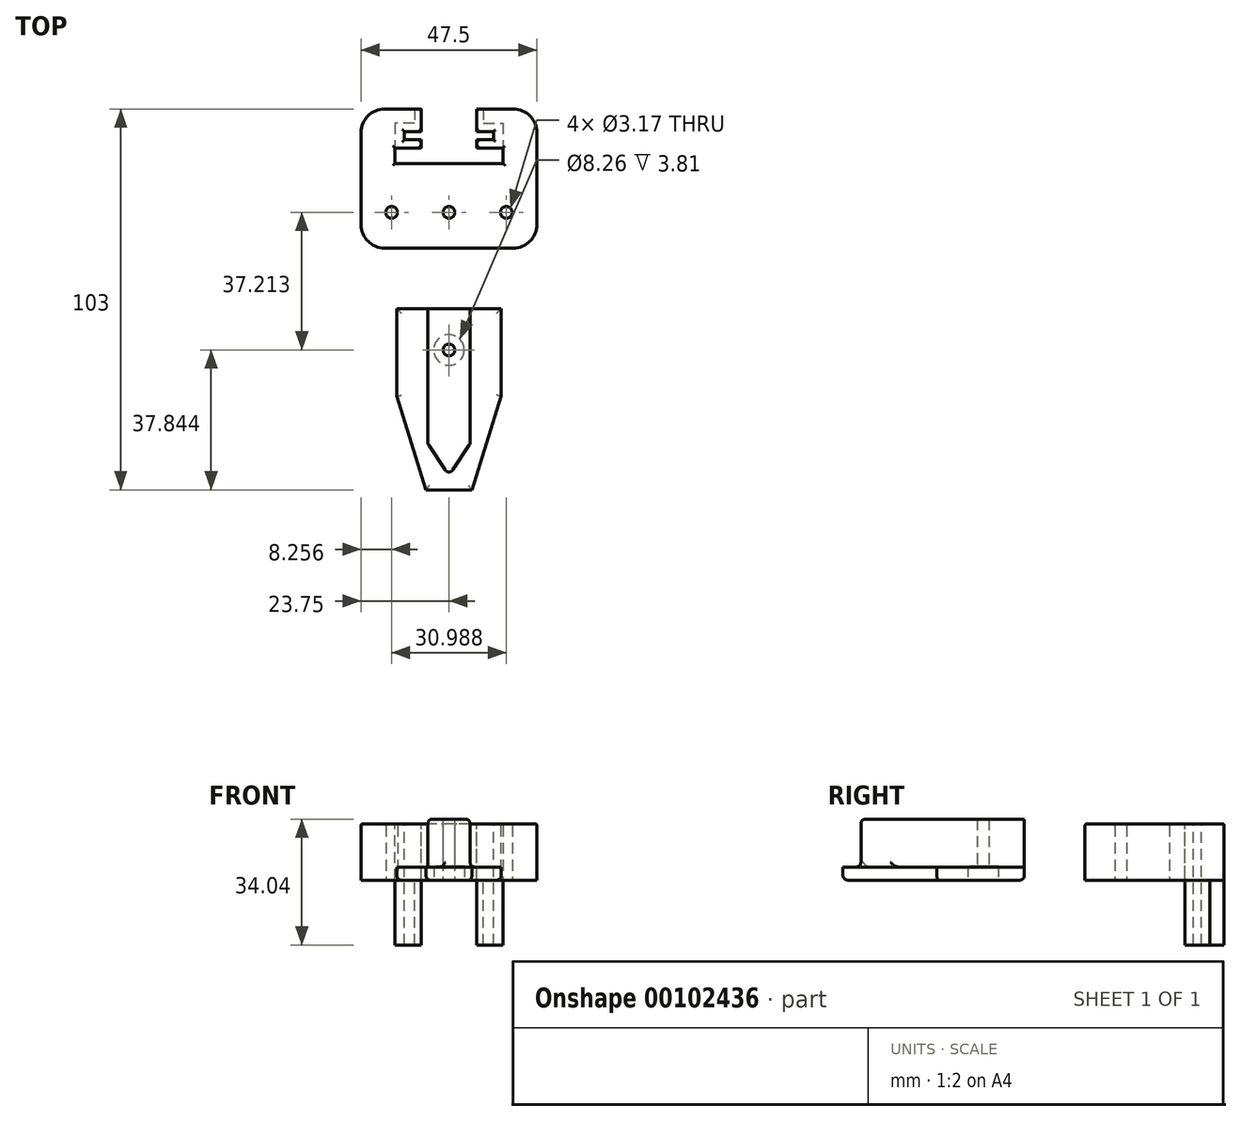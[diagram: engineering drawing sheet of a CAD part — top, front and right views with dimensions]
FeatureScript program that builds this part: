
annotation { "Feature Type Name" : "Feature", "Feature Type Description" : "" }
export const myFeature = defineFeature(function(context is Context, id is Id, definition is map)
    precondition{}
    {
        {
            var Q0;
            Q0=qCreatedBy(makeId("Top.planeOp"),FACE);
            var sketch = newSketch(context, id + "F0", { "sketchPlane" : qUnion([Q0])});
            skPoint(sketch, "E0.middle", {"position": v(0, 0) * mm});
            skLineSegment(sketch, "E1", {"start": v(-14.12, 0) * mm, "end": v(14.12, 0) * mm});
            skLineSegment(sketch, "E2", {"start": v(14.12, 0) * mm, "end": v(14.12, -23.62) * mm});
            skLineSegment(sketch, "E3", {"start": v(14.12, -23.62) * mm, "end": v(6.2, -49.02) * mm});
            skLineSegment(sketch, "E4", {"start": v(6.2, -49.02) * mm, "end": v(-6.2, -49.02) * mm});
            skLineSegment(sketch, "E5", {"start": v(-6.2, -49.02) * mm, "end": v(-14.12, -23.62) * mm});
            skLineSegment(sketch, "E6", {"start": v(-14.12, -23.62) * mm, "end": v(-14.12, 0) * mm});
            skLineSegment(sketch, "E7", {"start": v(0, 0) * mm, "end": v(0, -11.18) * mm, "construction": true});
            skCircle(sketch, "E8", {"center": v(0, -11.18) * mm, "radius": 4.13 * mm});
            skCircle(sketch, "E9", {"center": v(0, -11.18) * mm, "radius": 1.59 * mm});
            skLineSegment(sketch, "E10", {"start": v(5.71, 0) * mm, "end": v(5.71, -36.58) * mm});
            skLineSegment(sketch, "E11", {"start": v(5.72, -36.58) * mm, "end": v(0, -45.21) * mm});
            skLineSegment(sketch, "E12", {"start": v(0, -45.21) * mm, "end": v(-5.71, -36.58) * mm});
            skLineSegment(sketch, "E13", {"start": v(-5.72, -36.58) * mm, "end": v(-5.72, 0) * mm});
            skSolve(sketch);
        }
        {
            var Q0;
            {var subQ3=sQuery(id+"F0.wireOp",EDGE,"E2");Q0=makeQuery(id+"F0.imprint","IMPRINT",FACE,{"disambiguationData":[TD([[makeQuery(id+"F0.imprint","IMPRINT",EDGE,{"derivedFrom":subQ3}),-1.0]])]});}
            extrude(context, id + "F1", {"entities" : qUnion([Q0]), "depth" : 3.56 * mm});
        }
        {
            var Q0;
            Q0=makeQuery(id+"F0.imprint","IMPRINT",FACE,{"disambiguationData":[TD([[makeQuery(id+"F0.imprint","IMPRINT",EDGE,{"derivedFrom":sQuery(id+"F0.wireOp",EDGE,"E8")}),-1.0]])]});
            extrude(context, id + "F2", {"entities" : qUnion([Q0]), "operationType" : NewBodyOperationType.ADD, "depth" : 16.5 * mm});
        }
        {
            var Q0;
            Q0=makeQuery(id+"F0.imprint","IMPRINT",FACE,{"disambiguationData":[TD([[makeQuery(id+"F0.imprint","IMPRINT",EDGE,{"derivedFrom":sQuery(id+"F0.wireOp",EDGE,"E8")}),1.0]])]});
            extrude(context, id + "F3", {"entities" : qUnion([Q0]), "operationType" : NewBodyOperationType.ADD, "depth" : 16.5 * mm, "hasSecondDirection" : true, "secondDirectionOppositeDirection" : false, "secondDirectionDepth" : 3.8 * mm});
        }
        {
            var Q0;
            Q0=makeQuery(id+"F1.opExtrude","CAP_EDGE",EDGE,{"disambiguationData":[OSD([sQuery(id+"F0.wireOp",EDGE,"E4")])],"isStart":true});
            var Q1;
            Q1=makeQuery(id+"F1.opExtrude","CAP_EDGE",EDGE,{"disambiguationData":[OSD([sQuery(id+"F0.wireOp",EDGE,"E3")])],"isStart":true});
            var Q2;
            Q2=makeQuery(id+"F1.opExtrude","CAP_EDGE",EDGE,{"disambiguationData":[OSD([sQuery(id+"F0.wireOp",EDGE,"E2")])],"isStart":true});
            var Q3;
            {var subQ0=sQuery(id+"F0.wireOp",EDGE,"E1");Q3=makeQuery(id+"F2.boolean.opBoolean","MERGE",EDGE,{"derivedFrom":[makeQuery(id+"F1.opExtrude","CAP_EDGE",EDGE,{"disambiguationData":[OSD([subQ0]),TDD([makeQuery(id+"F0.imprint","IMPRINT",EDGE,{"disambiguationData":[TD([[makeQuery(id+"F0.imprint","INTERSECT",VERTEX,{"derivedFrom":[subQ0,sQuery(id+"F0.wireOp",EDGE,"E6")]}),-1.0]])],"derivedFrom":subQ0})])],"isStart":true}),makeQuery(id+"F1.opExtrude","CAP_EDGE",EDGE,{"disambiguationData":[OSD([subQ0]),TDD([makeQuery(id+"F0.imprint","IMPRINT",EDGE,{"disambiguationData":[TD([[makeQuery(id+"F0.imprint","INTERSECT",VERTEX,{"derivedFrom":[subQ0,sQuery(id+"F0.wireOp",EDGE,"E2")]}),1.0]])],"derivedFrom":subQ0})])],"isStart":true}),makeQuery(id+"F2.opExtrude","CAP_EDGE",EDGE,{"disambiguationData":[OSD([subQ0])],"isStart":true})]});}
            var Q4;
            Q4=makeQuery(id+"F1.opExtrude","CAP_EDGE",EDGE,{"disambiguationData":[OSD([sQuery(id+"F0.wireOp",EDGE,"E6")])],"isStart":true});
            var Q5;
            Q5=makeQuery(id+"F1.opExtrude","CAP_EDGE",EDGE,{"disambiguationData":[OSD([sQuery(id+"F0.wireOp",EDGE,"E5")])],"isStart":true});
            var Q6;
            Q6=makeQuery(id+"F2.opExtrude","CAP_EDGE",EDGE,{"disambiguationData":[OSD([sQuery(id+"F0.wireOp",EDGE,"E10")])],"isStart":false});
            var Q7;
            Q7=makeQuery(id+"F2.opExtrude","CAP_EDGE",EDGE,{"disambiguationData":[OSD([sQuery(id+"F0.wireOp",EDGE,"E13")])],"isStart":false});
            var Q8;
            Q8=makeQuery(id+"F2.opExtrude","SWEPT_EDGE",EDGE,{"disambiguationData":[OSD([sQuery(id+"F0.wireOp",EDGE,"E12"),sQuery(id+"F0.wireOp",EDGE,"E13")])]});
            var Q9;
            Q9=makeQuery(id+"F2.opExtrude","SWEPT_EDGE",EDGE,{"disambiguationData":[OSD([sQuery(id+"F0.wireOp",EDGE,"E10"),sQuery(id+"F0.wireOp",EDGE,"E11")])]});
            var Q10;
            Q10=makeQuery(id+"F2.opExtrude","SWEPT_FACE",FACE,{"disambiguationData":[OSD([sQuery(id+"F0.wireOp",EDGE,"E11")])]});
            var Q11;
            Q11=makeQuery(id+"F2.opExtrude","CAP_EDGE",EDGE,{"disambiguationData":[OSD([sQuery(id+"F0.wireOp",EDGE,"E12")])],"isStart":false});
            fillet(context, id + "F4", {"entities" : qUnion([Q0, Q1, Q2, Q3, Q4, Q5, Q6, Q7, Q8, Q9, Q10, Q11]), "radius" : 1.27 * mm, "tangentPropagation" : true, "allowEdgeOverflow" : false});
        }
        {
            var Q0;
            Q0=qCreatedBy(makeId("Top.planeOp"),FACE);
            var sketch = newSketch(context, id + "F5", { "sketchPlane" : qUnion([Q0])});
            skLineSegment(sketch, "E14", {"start": v(0, 16.39) * mm, "end": v(23.75, 16.39) * mm});
            skLineSegment(sketch, "E15", {"start": v(23.75, 16.39) * mm, "end": v(23.75, 53.98) * mm});
            skLineSegment(sketch, "E16", {"start": v(23.75, 53.98) * mm, "end": v(7.5, 53.98) * mm});
            skLineSegment(sketch, "E17", {"start": v(7.5, 53.98) * mm, "end": v(7.5, 47.88) * mm});
            skLineSegment(sketch, "E18", {"start": v(7.5, 47.88) * mm, "end": v(12.06, 47.88) * mm});
            skLineSegment(sketch, "E19", {"start": v(12.07, 47.88) * mm, "end": v(12.07, 45.67) * mm});
            skLineSegment(sketch, "E20", {"start": v(12.06, 45.67) * mm, "end": v(7.5, 45.67) * mm});
            skLineSegment(sketch, "E21", {"start": v(7.5, 45.67) * mm, "end": v(7.5, 43.44) * mm});
            skLineSegment(sketch, "E22", {"start": v(7.5, 43.44) * mm, "end": v(14.6, 43.44) * mm});
            skLineSegment(sketch, "E23", {"start": v(14.6, 43.44) * mm, "end": v(14.6, 39.25) * mm});
            skLineSegment(sketch, "E24", {"start": v(14.6, 39.25) * mm, "end": v(0, 39.25) * mm});
            skLineSegment(sketch, "E25", {"start": v(9.28, 53.98) * mm, "end": v(9.28, 50.17) * mm});
            skLineSegment(sketch, "E26", {"start": v(9.28, 50.17) * mm, "end": v(14.6, 50.17) * mm});
            skLineSegment(sketch, "E27", {"start": v(14.6, 50.17) * mm, "end": v(14.6, 43.44) * mm});
            skLineSegment(sketch, "E28.MirrorCS", {"start": v(23.75, 91.57) * mm, "end": v(23.75, 53.98) * mm});
            skLineSegment(sketch, "E29.MirrorCS", {"start": v(0, 91.57) * mm, "end": v(23.75, 91.57) * mm});
            skLineSegment(sketch, "E30.MirrorCS", {"start": v(0, 16.39) * mm, "end": v(-23.75, 16.39) * mm});
            skLineSegment(sketch, "E31.MirrorCS", {"start": v(-23.75, 16.39) * mm, "end": v(-23.75, 53.98) * mm});
            skLineSegment(sketch, "E32.MirrorCS", {"start": v(-23.75, 53.98) * mm, "end": v(-7.5, 53.98) * mm});
            skLineSegment(sketch, "E33.MirrorCS", {"start": v(-7.5, 53.98) * mm, "end": v(-7.5, 47.88) * mm});
            skLineSegment(sketch, "E34.MirrorCS", {"start": v(-7.5, 47.88) * mm, "end": v(-12.06, 47.88) * mm});
            skLineSegment(sketch, "E35.MirrorCS", {"start": v(-12.06, 45.67) * mm, "end": v(-7.5, 45.67) * mm});
            skLineSegment(sketch, "E36.MirrorCS", {"start": v(-7.5, 45.67) * mm, "end": v(-7.5, 43.44) * mm});
            skLineSegment(sketch, "E37.MirrorCS", {"start": v(-7.5, 43.44) * mm, "end": v(-14.6, 43.44) * mm});
            skLineSegment(sketch, "E38.MirrorCS", {"start": v(-14.6, 43.44) * mm, "end": v(-14.6, 39.25) * mm});
            skLineSegment(sketch, "E39.MirrorCS", {"start": v(-14.6, 39.25) * mm, "end": v(0, 39.25) * mm});
            skLineSegment(sketch, "E40.MirrorCS", {"start": v(-9.28, 53.98) * mm, "end": v(-9.28, 50.17) * mm});
            skLineSegment(sketch, "E41.MirrorCS", {"start": v(-9.28, 50.17) * mm, "end": v(-14.6, 50.17) * mm});
            skLineSegment(sketch, "E42.MirrorCS", {"start": v(-14.6, 50.17) * mm, "end": v(-14.6, 43.44) * mm});
            skLineSegment(sketch, "E43.MirrorCS", {"start": v(-12.07, 47.88) * mm, "end": v(-12.07, 45.67) * mm});
            skLineSegment(sketch, "E44.0", {"start": v(-17.78, 50.17) * mm, "end": v(-17.78, 43.44) * mm});
            skLineSegment(sketch, "E44.1", {"start": v(-17.78, 43.44) * mm, "end": v(-17.78, 36.07) * mm});
            skLineSegment(sketch, "E44.2", {"start": v(17.78, 50.17) * mm, "end": v(17.78, 43.44) * mm});
            skLineSegment(sketch, "E44.3", {"start": v(17.78, 43.44) * mm, "end": v(17.78, 36.07) * mm});
            skLineSegment(sketch, "E44.4", {"start": v(17.78, 36.07) * mm, "end": v(0, 36.07) * mm});
            skLineSegment(sketch, "E44.5", {"start": v(-17.78, 36.07) * mm, "end": v(0, 36.07) * mm});
            skLineSegment(sketch, "E45", {"start": v(14.6, 50.17) * mm, "end": v(17.78, 50.17) * mm});
            skLineSegment(sketch, "E46", {"start": v(-14.6, 50.17) * mm, "end": v(-17.78, 50.17) * mm});
            skLineSegment(sketch, "E47", {"start": v(0, 26.04) * mm, "end": v(15.5, 26.04) * mm, "construction": true});
            skCircle(sketch, "E48", {"center": v(0, 26.04) * mm, "radius": 1.59 * mm});
            skCircle(sketch, "E49", {"center": v(15.5, 26.04) * mm, "radius": 1.59 * mm});
            skCircle(sketch, "E50.MirrorC", {"center": v(-15.5, 26.04) * mm, "radius": 1.59 * mm});
            skSolve(sketch);
        }
        {
            var Q0;
            Q0=makeQuery(id+"F5.imprint","IMPRINT",FACE,{"disambiguationData":[TD([[makeQuery(id+"F5.imprint","IMPRINT",EDGE,{"derivedFrom":sQuery(id+"F5.wireOp",EDGE,"E14")}),1.0]])]});
            extrude(context, id + "F6", {"entities" : qUnion([Q0]), "depth" : 15.24 * mm});
        }
        {
            var Q0;
            Q0=makeQuery(id+"F5.imprint","IMPRINT",FACE,{"disambiguationData":[TD([[makeQuery(id+"F5.imprint","IMPRINT",EDGE,{"derivedFrom":sQuery(id+"F5.wireOp",EDGE,"E23")}),1.0]])]});
            extrude(context, id + "F7", {"entities" : qUnion([Q0]), "operationType" : NewBodyOperationType.ADD, "depth" : 15.24 * mm});
        }
        {
            var Q0;
            {var subQ0=sQuery(id+"F5.wireOp",EDGE,"E33.MirrorCS");Q0=makeQuery(id+"F5.imprint","IMPRINT",FACE,{"disambiguationData":[TD([[makeQuery(id+"F5.imprint","IMPRINT",EDGE,{"derivedFrom":subQ0}),-1.0]])]});}
            var Q1;
            {var subQ0=sQuery(id+"F5.wireOp",EDGE,"E17");Q1=makeQuery(id+"F5.imprint","IMPRINT",FACE,{"disambiguationData":[TD([[makeQuery(id+"F5.imprint","IMPRINT",EDGE,{"derivedFrom":subQ0}),1.0]])]});}
            extrude(context, id + "F8", {"entities" : qUnion([Q0, Q1]), "operationType" : NewBodyOperationType.ADD, "oppositeDirection" : true, "depth" : 17.53 * mm, "hasSecondDirection" : true, "secondDirectionOppositeDirection" : false, "secondDirectionDepth" : 15.24 * mm});
        }
        {
            var Q0;
            Q0=makeQuery(id+"F6.opExtrude","SWEPT_EDGE",EDGE,{"disambiguationData":[OSD([sQuery(id+"F5.wireOp",EDGE,"E15"),sQuery(id+"F5.wireOp",EDGE,"E16")])]});
            var Q1;
            Q1=makeQuery(id+"F6.opExtrude","SWEPT_EDGE",EDGE,{"disambiguationData":[OSD([sQuery(id+"F5.wireOp",EDGE,"E14"),sQuery(id+"F5.wireOp",EDGE,"E15")])]});
            var Q2;
            Q2=makeQuery(id+"F6.opExtrude","SWEPT_EDGE",EDGE,{"disambiguationData":[OSD([sQuery(id+"F5.wireOp",EDGE,"E31.MirrorCS"),sQuery(id+"F5.wireOp",EDGE,"E32.MirrorCS")])]});
            var Q3;
            Q3=makeQuery(id+"F6.opExtrude","SWEPT_EDGE",EDGE,{"disambiguationData":[OSD([sQuery(id+"F5.wireOp",EDGE,"E30.MirrorCS"),sQuery(id+"F5.wireOp",EDGE,"E31.MirrorCS")])]});
            fillet(context, id + "F9", {"entities" : qUnion([Q0, Q1, Q2, Q3]), "radius" : 6.35 * mm, "tangentPropagation" : true, "allowEdgeOverflow" : false});
        }
        {
            var Q0;
            {var subQ0=sQuery(id+"F5.wireOp",EDGE,"E16");Q0=makeQuery(id+"F8.boolean.opBoolean","MERGE",EDGE,{"derivedFrom":[makeQuery(id+"F6.opExtrude","CAP_EDGE",EDGE,{"disambiguationData":[OSD([subQ0])],"isStart":false}),makeQuery(id+"F8.opExtrude","CAP_EDGE",EDGE,{"disambiguationData":[OSD([subQ0])],"isStart":true})]});}
            var Q1;
            {var subQ0=sQuery(id+"F5.wireOp",EDGE,"E42.MirrorCS");var subQ1=sQuery(id+"F5.wireOp",EDGE,"E41.MirrorCS");var subQ2=sQuery(id+"F5.wireOp",EDGE,"E40.MirrorCS");var subQ3=sQuery(id+"F5.wireOp",EDGE,"E32.MirrorCS");var subQ4=sQuery(id+"F5.wireOp",EDGE,"E27");var subQ5=sQuery(id+"F5.wireOp",EDGE,"E26");var subQ6=sQuery(id+"F5.wireOp",EDGE,"E25");var subQ7=sQuery(id+"F5.wireOp",EDGE,"E16");var subQ8=sQuery(id+"F5.wireOp",EDGE,"E46");var subQ9=sQuery(id+"F5.wireOp",EDGE,"E45");var subQ10=sQuery(id+"F5.wireOp",EDGE,"E44.5");var subQ11=sQuery(id+"F5.wireOp",EDGE,"E44.4");var subQ12=sQuery(id+"F5.wireOp",EDGE,"E44.3");var subQ13=sQuery(id+"F5.wireOp",EDGE,"E44.2");var subQ14=sQuery(id+"F5.wireOp",EDGE,"E44.1");var subQ15=sQuery(id+"F5.wireOp",EDGE,"E44.0");var subQ16=sQuery(id+"F5.wireOp",EDGE,"E15");Q1=makeQuery(id+"F9.opFillet","BLEND_EDGE",EDGE,{"blendedFrom":[makeQuery(id+"F6.opExtrude","SWEPT_EDGE",EDGE,{"disambiguationData":[OSD([subQ16,subQ7])]}),makeQuery(id+"F8.boolean.opBoolean","MERGE",FACE,{"derivedFrom":[makeQuery(id+"F7.boolean.opBoolean","MERGE",FACE,{"derivedFrom":[makeQuery(id+"F6.opExtrude","CAP_FACE",FACE,{"disambiguationData":[OSD([sQuery(id+"F5.wireOp",EDGE,"E14"),subQ16,subQ7,subQ6,subQ5,sQuery(id+"F5.wireOp",EDGE,"E30.MirrorCS"),sQuery(id+"F5.wireOp",EDGE,"E31.MirrorCS"),subQ3,subQ2,subQ1,subQ15,subQ14,subQ13,subQ12,subQ11,subQ10,subQ9,subQ8,sQuery(id+"F5.wireOp",EDGE,"E48"),sQuery(id+"F5.wireOp",EDGE,"E49"),sQuery(id+"F5.wireOp",EDGE,"E50.MirrorC")])],"isStart":false}),makeQuery(id+"F7.opExtrude","CAP_FACE",FACE,{"disambiguationData":[OSD([sQuery(id+"F5.wireOp",EDGE,"E23"),sQuery(id+"F5.wireOp",EDGE,"E24"),subQ4,sQuery(id+"F5.wireOp",EDGE,"E38.MirrorCS"),sQuery(id+"F5.wireOp",EDGE,"E39.MirrorCS"),subQ0,subQ15,subQ14,subQ13,subQ12,subQ11,subQ10,subQ9,subQ8])],"isStart":false})]}),makeQuery(id+"F8.opExtrude","CAP_FACE",FACE,{"disambiguationData":[OSD([subQ7,sQuery(id+"F5.wireOp",EDGE,"E17"),sQuery(id+"F5.wireOp",EDGE,"E18"),sQuery(id+"F5.wireOp",EDGE,"E19"),sQuery(id+"F5.wireOp",EDGE,"E20"),sQuery(id+"F5.wireOp",EDGE,"E21"),sQuery(id+"F5.wireOp",EDGE,"E22"),subQ6,subQ5,subQ4])],"isStart":true}),makeQuery(id+"F8.opExtrude","CAP_FACE",FACE,{"disambiguationData":[OSD([subQ3,sQuery(id+"F5.wireOp",EDGE,"E33.MirrorCS"),sQuery(id+"F5.wireOp",EDGE,"E34.MirrorCS"),sQuery(id+"F5.wireOp",EDGE,"E35.MirrorCS"),sQuery(id+"F5.wireOp",EDGE,"E36.MirrorCS"),sQuery(id+"F5.wireOp",EDGE,"E37.MirrorCS"),subQ2,subQ1,subQ0,sQuery(id+"F5.wireOp",EDGE,"E43.MirrorCS")])],"isStart":true})]})],"blendedInto":[makeQuery(id+"F8.boolean.opBoolean","MERGE",FACE,{"derivedFrom":[makeQuery(id+"F7.boolean.opBoolean","MERGE",FACE,{"derivedFrom":[makeQuery(id+"F6.opExtrude","CAP_FACE",FACE,{"disambiguationData":[OSD([sQuery(id+"F5.wireOp",EDGE,"E14"),subQ16,subQ7,subQ6,subQ5,sQuery(id+"F5.wireOp",EDGE,"E30.MirrorCS"),sQuery(id+"F5.wireOp",EDGE,"E31.MirrorCS"),subQ3,subQ2,subQ1,subQ15,subQ14,subQ13,subQ12,subQ11,subQ10,subQ9,subQ8,sQuery(id+"F5.wireOp",EDGE,"E48"),sQuery(id+"F5.wireOp",EDGE,"E49"),sQuery(id+"F5.wireOp",EDGE,"E50.MirrorC")])],"isStart":false}),makeQuery(id+"F7.opExtrude","CAP_FACE",FACE,{"disambiguationData":[OSD([sQuery(id+"F5.wireOp",EDGE,"E23"),sQuery(id+"F5.wireOp",EDGE,"E24"),subQ4,sQuery(id+"F5.wireOp",EDGE,"E38.MirrorCS"),sQuery(id+"F5.wireOp",EDGE,"E39.MirrorCS"),subQ0,subQ15,subQ14,subQ13,subQ12,subQ11,subQ10,subQ9,subQ8])],"isStart":false})]}),makeQuery(id+"F8.opExtrude","CAP_FACE",FACE,{"disambiguationData":[OSD([subQ7,sQuery(id+"F5.wireOp",EDGE,"E17"),sQuery(id+"F5.wireOp",EDGE,"E18"),sQuery(id+"F5.wireOp",EDGE,"E19"),sQuery(id+"F5.wireOp",EDGE,"E20"),sQuery(id+"F5.wireOp",EDGE,"E21"),sQuery(id+"F5.wireOp",EDGE,"E22"),subQ6,subQ5,subQ4])],"isStart":true}),makeQuery(id+"F8.opExtrude","CAP_FACE",FACE,{"disambiguationData":[OSD([subQ3,sQuery(id+"F5.wireOp",EDGE,"E33.MirrorCS"),sQuery(id+"F5.wireOp",EDGE,"E34.MirrorCS"),sQuery(id+"F5.wireOp",EDGE,"E35.MirrorCS"),sQuery(id+"F5.wireOp",EDGE,"E36.MirrorCS"),sQuery(id+"F5.wireOp",EDGE,"E37.MirrorCS"),subQ2,subQ1,subQ0,sQuery(id+"F5.wireOp",EDGE,"E43.MirrorCS")])],"isStart":true})]})]});}
            var Q2;
            Q2=makeQuery(id+"F6.opExtrude","CAP_EDGE",EDGE,{"disambiguationData":[OSD([sQuery(id+"F5.wireOp",EDGE,"E15")])],"isStart":false});
            var Q3;
            {var subQ0=sQuery(id+"F5.wireOp",EDGE,"E42.MirrorCS");var subQ1=sQuery(id+"F5.wireOp",EDGE,"E41.MirrorCS");var subQ2=sQuery(id+"F5.wireOp",EDGE,"E40.MirrorCS");var subQ3=sQuery(id+"F5.wireOp",EDGE,"E32.MirrorCS");var subQ4=sQuery(id+"F5.wireOp",EDGE,"E27");var subQ5=sQuery(id+"F5.wireOp",EDGE,"E26");var subQ6=sQuery(id+"F5.wireOp",EDGE,"E25");var subQ7=sQuery(id+"F5.wireOp",EDGE,"E16");var subQ8=sQuery(id+"F5.wireOp",EDGE,"E46");var subQ9=sQuery(id+"F5.wireOp",EDGE,"E45");var subQ10=sQuery(id+"F5.wireOp",EDGE,"E44.5");var subQ11=sQuery(id+"F5.wireOp",EDGE,"E44.4");var subQ12=sQuery(id+"F5.wireOp",EDGE,"E44.3");var subQ13=sQuery(id+"F5.wireOp",EDGE,"E44.2");var subQ14=sQuery(id+"F5.wireOp",EDGE,"E44.1");var subQ15=sQuery(id+"F5.wireOp",EDGE,"E44.0");var subQ16=sQuery(id+"F5.wireOp",EDGE,"E15");var subQ17=sQuery(id+"F5.wireOp",EDGE,"E14");Q3=makeQuery(id+"F9.opFillet","BLEND_EDGE",EDGE,{"blendedFrom":[makeQuery(id+"F6.opExtrude","SWEPT_EDGE",EDGE,{"disambiguationData":[OSD([subQ17,subQ16])]}),makeQuery(id+"F8.boolean.opBoolean","MERGE",FACE,{"derivedFrom":[makeQuery(id+"F7.boolean.opBoolean","MERGE",FACE,{"derivedFrom":[makeQuery(id+"F6.opExtrude","CAP_FACE",FACE,{"disambiguationData":[OSD([subQ17,subQ16,subQ7,subQ6,subQ5,sQuery(id+"F5.wireOp",EDGE,"E30.MirrorCS"),sQuery(id+"F5.wireOp",EDGE,"E31.MirrorCS"),subQ3,subQ2,subQ1,subQ15,subQ14,subQ13,subQ12,subQ11,subQ10,subQ9,subQ8,sQuery(id+"F5.wireOp",EDGE,"E48"),sQuery(id+"F5.wireOp",EDGE,"E49"),sQuery(id+"F5.wireOp",EDGE,"E50.MirrorC")])],"isStart":false}),makeQuery(id+"F7.opExtrude","CAP_FACE",FACE,{"disambiguationData":[OSD([sQuery(id+"F5.wireOp",EDGE,"E23"),sQuery(id+"F5.wireOp",EDGE,"E24"),subQ4,sQuery(id+"F5.wireOp",EDGE,"E38.MirrorCS"),sQuery(id+"F5.wireOp",EDGE,"E39.MirrorCS"),subQ0,subQ15,subQ14,subQ13,subQ12,subQ11,subQ10,subQ9,subQ8])],"isStart":false})]}),makeQuery(id+"F8.opExtrude","CAP_FACE",FACE,{"disambiguationData":[OSD([subQ7,sQuery(id+"F5.wireOp",EDGE,"E17"),sQuery(id+"F5.wireOp",EDGE,"E18"),sQuery(id+"F5.wireOp",EDGE,"E19"),sQuery(id+"F5.wireOp",EDGE,"E20"),sQuery(id+"F5.wireOp",EDGE,"E21"),sQuery(id+"F5.wireOp",EDGE,"E22"),subQ6,subQ5,subQ4])],"isStart":true}),makeQuery(id+"F8.opExtrude","CAP_FACE",FACE,{"disambiguationData":[OSD([subQ3,sQuery(id+"F5.wireOp",EDGE,"E33.MirrorCS"),sQuery(id+"F5.wireOp",EDGE,"E34.MirrorCS"),sQuery(id+"F5.wireOp",EDGE,"E35.MirrorCS"),sQuery(id+"F5.wireOp",EDGE,"E36.MirrorCS"),sQuery(id+"F5.wireOp",EDGE,"E37.MirrorCS"),subQ2,subQ1,subQ0,sQuery(id+"F5.wireOp",EDGE,"E43.MirrorCS")])],"isStart":true})]})],"blendedInto":[makeQuery(id+"F8.boolean.opBoolean","MERGE",FACE,{"derivedFrom":[makeQuery(id+"F7.boolean.opBoolean","MERGE",FACE,{"derivedFrom":[makeQuery(id+"F6.opExtrude","CAP_FACE",FACE,{"disambiguationData":[OSD([subQ17,subQ16,subQ7,subQ6,subQ5,sQuery(id+"F5.wireOp",EDGE,"E30.MirrorCS"),sQuery(id+"F5.wireOp",EDGE,"E31.MirrorCS"),subQ3,subQ2,subQ1,subQ15,subQ14,subQ13,subQ12,subQ11,subQ10,subQ9,subQ8,sQuery(id+"F5.wireOp",EDGE,"E48"),sQuery(id+"F5.wireOp",EDGE,"E49"),sQuery(id+"F5.wireOp",EDGE,"E50.MirrorC")])],"isStart":false}),makeQuery(id+"F7.opExtrude","CAP_FACE",FACE,{"disambiguationData":[OSD([sQuery(id+"F5.wireOp",EDGE,"E23"),sQuery(id+"F5.wireOp",EDGE,"E24"),subQ4,sQuery(id+"F5.wireOp",EDGE,"E38.MirrorCS"),sQuery(id+"F5.wireOp",EDGE,"E39.MirrorCS"),subQ0,subQ15,subQ14,subQ13,subQ12,subQ11,subQ10,subQ9,subQ8])],"isStart":false})]}),makeQuery(id+"F8.opExtrude","CAP_FACE",FACE,{"disambiguationData":[OSD([subQ7,sQuery(id+"F5.wireOp",EDGE,"E17"),sQuery(id+"F5.wireOp",EDGE,"E18"),sQuery(id+"F5.wireOp",EDGE,"E19"),sQuery(id+"F5.wireOp",EDGE,"E20"),sQuery(id+"F5.wireOp",EDGE,"E21"),sQuery(id+"F5.wireOp",EDGE,"E22"),subQ6,subQ5,subQ4])],"isStart":true}),makeQuery(id+"F8.opExtrude","CAP_FACE",FACE,{"disambiguationData":[OSD([subQ3,sQuery(id+"F5.wireOp",EDGE,"E33.MirrorCS"),sQuery(id+"F5.wireOp",EDGE,"E34.MirrorCS"),sQuery(id+"F5.wireOp",EDGE,"E35.MirrorCS"),sQuery(id+"F5.wireOp",EDGE,"E36.MirrorCS"),sQuery(id+"F5.wireOp",EDGE,"E37.MirrorCS"),subQ2,subQ1,subQ0,sQuery(id+"F5.wireOp",EDGE,"E43.MirrorCS")])],"isStart":true})]})]});}
            var Q4;
            Q4=makeQuery(id+"F6.opExtrude","CAP_EDGE",EDGE,{"disambiguationData":[OSD([sQuery(id+"F5.wireOp",EDGE,"E14"),sQuery(id+"F5.wireOp",EDGE,"E30.MirrorCS")])],"isStart":false});
            var Q5;
            {var subQ0=sQuery(id+"F5.wireOp",EDGE,"E42.MirrorCS");var subQ1=sQuery(id+"F5.wireOp",EDGE,"E41.MirrorCS");var subQ2=sQuery(id+"F5.wireOp",EDGE,"E40.MirrorCS");var subQ3=sQuery(id+"F5.wireOp",EDGE,"E32.MirrorCS");var subQ4=sQuery(id+"F5.wireOp",EDGE,"E27");var subQ5=sQuery(id+"F5.wireOp",EDGE,"E26");var subQ6=sQuery(id+"F5.wireOp",EDGE,"E25");var subQ7=sQuery(id+"F5.wireOp",EDGE,"E16");var subQ8=sQuery(id+"F5.wireOp",EDGE,"E46");var subQ9=sQuery(id+"F5.wireOp",EDGE,"E45");var subQ10=sQuery(id+"F5.wireOp",EDGE,"E44.5");var subQ11=sQuery(id+"F5.wireOp",EDGE,"E44.4");var subQ12=sQuery(id+"F5.wireOp",EDGE,"E44.3");var subQ13=sQuery(id+"F5.wireOp",EDGE,"E44.2");var subQ14=sQuery(id+"F5.wireOp",EDGE,"E44.1");var subQ15=sQuery(id+"F5.wireOp",EDGE,"E44.0");var subQ16=sQuery(id+"F5.wireOp",EDGE,"E31.MirrorCS");var subQ17=sQuery(id+"F5.wireOp",EDGE,"E30.MirrorCS");Q5=makeQuery(id+"F9.opFillet","BLEND_EDGE",EDGE,{"blendedFrom":[makeQuery(id+"F6.opExtrude","SWEPT_EDGE",EDGE,{"disambiguationData":[OSD([subQ17,subQ16])]}),makeQuery(id+"F8.boolean.opBoolean","MERGE",FACE,{"derivedFrom":[makeQuery(id+"F7.boolean.opBoolean","MERGE",FACE,{"derivedFrom":[makeQuery(id+"F6.opExtrude","CAP_FACE",FACE,{"disambiguationData":[OSD([sQuery(id+"F5.wireOp",EDGE,"E14"),sQuery(id+"F5.wireOp",EDGE,"E15"),subQ7,subQ6,subQ5,subQ17,subQ16,subQ3,subQ2,subQ1,subQ15,subQ14,subQ13,subQ12,subQ11,subQ10,subQ9,subQ8,sQuery(id+"F5.wireOp",EDGE,"E48"),sQuery(id+"F5.wireOp",EDGE,"E49"),sQuery(id+"F5.wireOp",EDGE,"E50.MirrorC")])],"isStart":false}),makeQuery(id+"F7.opExtrude","CAP_FACE",FACE,{"disambiguationData":[OSD([sQuery(id+"F5.wireOp",EDGE,"E23"),sQuery(id+"F5.wireOp",EDGE,"E24"),subQ4,sQuery(id+"F5.wireOp",EDGE,"E38.MirrorCS"),sQuery(id+"F5.wireOp",EDGE,"E39.MirrorCS"),subQ0,subQ15,subQ14,subQ13,subQ12,subQ11,subQ10,subQ9,subQ8])],"isStart":false})]}),makeQuery(id+"F8.opExtrude","CAP_FACE",FACE,{"disambiguationData":[OSD([subQ7,sQuery(id+"F5.wireOp",EDGE,"E17"),sQuery(id+"F5.wireOp",EDGE,"E18"),sQuery(id+"F5.wireOp",EDGE,"E19"),sQuery(id+"F5.wireOp",EDGE,"E20"),sQuery(id+"F5.wireOp",EDGE,"E21"),sQuery(id+"F5.wireOp",EDGE,"E22"),subQ6,subQ5,subQ4])],"isStart":true}),makeQuery(id+"F8.opExtrude","CAP_FACE",FACE,{"disambiguationData":[OSD([subQ3,sQuery(id+"F5.wireOp",EDGE,"E33.MirrorCS"),sQuery(id+"F5.wireOp",EDGE,"E34.MirrorCS"),sQuery(id+"F5.wireOp",EDGE,"E35.MirrorCS"),sQuery(id+"F5.wireOp",EDGE,"E36.MirrorCS"),sQuery(id+"F5.wireOp",EDGE,"E37.MirrorCS"),subQ2,subQ1,subQ0,sQuery(id+"F5.wireOp",EDGE,"E43.MirrorCS")])],"isStart":true})]})],"blendedInto":[makeQuery(id+"F8.boolean.opBoolean","MERGE",FACE,{"derivedFrom":[makeQuery(id+"F7.boolean.opBoolean","MERGE",FACE,{"derivedFrom":[makeQuery(id+"F6.opExtrude","CAP_FACE",FACE,{"disambiguationData":[OSD([sQuery(id+"F5.wireOp",EDGE,"E14"),sQuery(id+"F5.wireOp",EDGE,"E15"),subQ7,subQ6,subQ5,subQ17,subQ16,subQ3,subQ2,subQ1,subQ15,subQ14,subQ13,subQ12,subQ11,subQ10,subQ9,subQ8,sQuery(id+"F5.wireOp",EDGE,"E48"),sQuery(id+"F5.wireOp",EDGE,"E49"),sQuery(id+"F5.wireOp",EDGE,"E50.MirrorC")])],"isStart":false}),makeQuery(id+"F7.opExtrude","CAP_FACE",FACE,{"disambiguationData":[OSD([sQuery(id+"F5.wireOp",EDGE,"E23"),sQuery(id+"F5.wireOp",EDGE,"E24"),subQ4,sQuery(id+"F5.wireOp",EDGE,"E38.MirrorCS"),sQuery(id+"F5.wireOp",EDGE,"E39.MirrorCS"),subQ0,subQ15,subQ14,subQ13,subQ12,subQ11,subQ10,subQ9,subQ8])],"isStart":false})]}),makeQuery(id+"F8.opExtrude","CAP_FACE",FACE,{"disambiguationData":[OSD([subQ7,sQuery(id+"F5.wireOp",EDGE,"E17"),sQuery(id+"F5.wireOp",EDGE,"E18"),sQuery(id+"F5.wireOp",EDGE,"E19"),sQuery(id+"F5.wireOp",EDGE,"E20"),sQuery(id+"F5.wireOp",EDGE,"E21"),sQuery(id+"F5.wireOp",EDGE,"E22"),subQ6,subQ5,subQ4])],"isStart":true}),makeQuery(id+"F8.opExtrude","CAP_FACE",FACE,{"disambiguationData":[OSD([subQ3,sQuery(id+"F5.wireOp",EDGE,"E33.MirrorCS"),sQuery(id+"F5.wireOp",EDGE,"E34.MirrorCS"),sQuery(id+"F5.wireOp",EDGE,"E35.MirrorCS"),sQuery(id+"F5.wireOp",EDGE,"E36.MirrorCS"),sQuery(id+"F5.wireOp",EDGE,"E37.MirrorCS"),subQ2,subQ1,subQ0,sQuery(id+"F5.wireOp",EDGE,"E43.MirrorCS")])],"isStart":true})]})]});}
            var Q6;
            Q6=makeQuery(id+"F6.opExtrude","CAP_EDGE",EDGE,{"disambiguationData":[OSD([sQuery(id+"F5.wireOp",EDGE,"E31.MirrorCS")])],"isStart":false});
            var Q7;
            {var subQ0=sQuery(id+"F5.wireOp",EDGE,"E42.MirrorCS");var subQ1=sQuery(id+"F5.wireOp",EDGE,"E41.MirrorCS");var subQ2=sQuery(id+"F5.wireOp",EDGE,"E40.MirrorCS");var subQ3=sQuery(id+"F5.wireOp",EDGE,"E32.MirrorCS");var subQ4=sQuery(id+"F5.wireOp",EDGE,"E27");var subQ5=sQuery(id+"F5.wireOp",EDGE,"E26");var subQ6=sQuery(id+"F5.wireOp",EDGE,"E25");var subQ7=sQuery(id+"F5.wireOp",EDGE,"E16");var subQ8=sQuery(id+"F5.wireOp",EDGE,"E46");var subQ9=sQuery(id+"F5.wireOp",EDGE,"E45");var subQ10=sQuery(id+"F5.wireOp",EDGE,"E44.5");var subQ11=sQuery(id+"F5.wireOp",EDGE,"E44.4");var subQ12=sQuery(id+"F5.wireOp",EDGE,"E44.3");var subQ13=sQuery(id+"F5.wireOp",EDGE,"E44.2");var subQ14=sQuery(id+"F5.wireOp",EDGE,"E44.1");var subQ15=sQuery(id+"F5.wireOp",EDGE,"E44.0");var subQ16=sQuery(id+"F5.wireOp",EDGE,"E31.MirrorCS");Q7=makeQuery(id+"F9.opFillet","BLEND_EDGE",EDGE,{"blendedFrom":[makeQuery(id+"F6.opExtrude","SWEPT_EDGE",EDGE,{"disambiguationData":[OSD([subQ16,subQ3])]}),makeQuery(id+"F8.boolean.opBoolean","MERGE",FACE,{"derivedFrom":[makeQuery(id+"F7.boolean.opBoolean","MERGE",FACE,{"derivedFrom":[makeQuery(id+"F6.opExtrude","CAP_FACE",FACE,{"disambiguationData":[OSD([sQuery(id+"F5.wireOp",EDGE,"E14"),sQuery(id+"F5.wireOp",EDGE,"E15"),subQ7,subQ6,subQ5,sQuery(id+"F5.wireOp",EDGE,"E30.MirrorCS"),subQ16,subQ3,subQ2,subQ1,subQ15,subQ14,subQ13,subQ12,subQ11,subQ10,subQ9,subQ8,sQuery(id+"F5.wireOp",EDGE,"E48"),sQuery(id+"F5.wireOp",EDGE,"E49"),sQuery(id+"F5.wireOp",EDGE,"E50.MirrorC")])],"isStart":false}),makeQuery(id+"F7.opExtrude","CAP_FACE",FACE,{"disambiguationData":[OSD([sQuery(id+"F5.wireOp",EDGE,"E23"),sQuery(id+"F5.wireOp",EDGE,"E24"),subQ4,sQuery(id+"F5.wireOp",EDGE,"E38.MirrorCS"),sQuery(id+"F5.wireOp",EDGE,"E39.MirrorCS"),subQ0,subQ15,subQ14,subQ13,subQ12,subQ11,subQ10,subQ9,subQ8])],"isStart":false})]}),makeQuery(id+"F8.opExtrude","CAP_FACE",FACE,{"disambiguationData":[OSD([subQ7,sQuery(id+"F5.wireOp",EDGE,"E17"),sQuery(id+"F5.wireOp",EDGE,"E18"),sQuery(id+"F5.wireOp",EDGE,"E19"),sQuery(id+"F5.wireOp",EDGE,"E20"),sQuery(id+"F5.wireOp",EDGE,"E21"),sQuery(id+"F5.wireOp",EDGE,"E22"),subQ6,subQ5,subQ4])],"isStart":true}),makeQuery(id+"F8.opExtrude","CAP_FACE",FACE,{"disambiguationData":[OSD([subQ3,sQuery(id+"F5.wireOp",EDGE,"E33.MirrorCS"),sQuery(id+"F5.wireOp",EDGE,"E34.MirrorCS"),sQuery(id+"F5.wireOp",EDGE,"E35.MirrorCS"),sQuery(id+"F5.wireOp",EDGE,"E36.MirrorCS"),sQuery(id+"F5.wireOp",EDGE,"E37.MirrorCS"),subQ2,subQ1,subQ0,sQuery(id+"F5.wireOp",EDGE,"E43.MirrorCS")])],"isStart":true})]})],"blendedInto":[makeQuery(id+"F8.boolean.opBoolean","MERGE",FACE,{"derivedFrom":[makeQuery(id+"F7.boolean.opBoolean","MERGE",FACE,{"derivedFrom":[makeQuery(id+"F6.opExtrude","CAP_FACE",FACE,{"disambiguationData":[OSD([sQuery(id+"F5.wireOp",EDGE,"E14"),sQuery(id+"F5.wireOp",EDGE,"E15"),subQ7,subQ6,subQ5,sQuery(id+"F5.wireOp",EDGE,"E30.MirrorCS"),subQ16,subQ3,subQ2,subQ1,subQ15,subQ14,subQ13,subQ12,subQ11,subQ10,subQ9,subQ8,sQuery(id+"F5.wireOp",EDGE,"E48"),sQuery(id+"F5.wireOp",EDGE,"E49"),sQuery(id+"F5.wireOp",EDGE,"E50.MirrorC")])],"isStart":false}),makeQuery(id+"F7.opExtrude","CAP_FACE",FACE,{"disambiguationData":[OSD([sQuery(id+"F5.wireOp",EDGE,"E23"),sQuery(id+"F5.wireOp",EDGE,"E24"),subQ4,sQuery(id+"F5.wireOp",EDGE,"E38.MirrorCS"),sQuery(id+"F5.wireOp",EDGE,"E39.MirrorCS"),subQ0,subQ15,subQ14,subQ13,subQ12,subQ11,subQ10,subQ9,subQ8])],"isStart":false})]}),makeQuery(id+"F8.opExtrude","CAP_FACE",FACE,{"disambiguationData":[OSD([subQ7,sQuery(id+"F5.wireOp",EDGE,"E17"),sQuery(id+"F5.wireOp",EDGE,"E18"),sQuery(id+"F5.wireOp",EDGE,"E19"),sQuery(id+"F5.wireOp",EDGE,"E20"),sQuery(id+"F5.wireOp",EDGE,"E21"),sQuery(id+"F5.wireOp",EDGE,"E22"),subQ6,subQ5,subQ4])],"isStart":true}),makeQuery(id+"F8.opExtrude","CAP_FACE",FACE,{"disambiguationData":[OSD([subQ3,sQuery(id+"F5.wireOp",EDGE,"E33.MirrorCS"),sQuery(id+"F5.wireOp",EDGE,"E34.MirrorCS"),sQuery(id+"F5.wireOp",EDGE,"E35.MirrorCS"),sQuery(id+"F5.wireOp",EDGE,"E36.MirrorCS"),sQuery(id+"F5.wireOp",EDGE,"E37.MirrorCS"),subQ2,subQ1,subQ0,sQuery(id+"F5.wireOp",EDGE,"E43.MirrorCS")])],"isStart":true})]})]});}
            var Q8;
            Q8=makeQuery(id+"F7.opExtrude","CAP_EDGE",EDGE,{"disambiguationData":[OSD([sQuery(id+"F5.wireOp",EDGE,"E38.MirrorCS"),sQuery(id+"F5.wireOp",EDGE,"E42.MirrorCS")])],"isStart":false});
            var Q9;
            Q9=makeQuery(id+"F7.opExtrude","CAP_EDGE",EDGE,{"disambiguationData":[OSD([sQuery(id+"F5.wireOp",EDGE,"E24"),sQuery(id+"F5.wireOp",EDGE,"E39.MirrorCS")])],"isStart":false});
            var Q10;
            Q10=makeQuery(id+"F7.opExtrude","CAP_EDGE",EDGE,{"disambiguationData":[OSD([sQuery(id+"F5.wireOp",EDGE,"E23"),sQuery(id+"F5.wireOp",EDGE,"E27")])],"isStart":false});
            var Q11;
            Q11=makeQuery(id+"F8.opExtrude","CAP_EDGE",EDGE,{"disambiguationData":[OSD([sQuery(id+"F5.wireOp",EDGE,"E22")])],"isStart":true});
            var Q12;
            Q12=makeQuery(id+"F8.opExtrude","CAP_EDGE",EDGE,{"disambiguationData":[OSD([sQuery(id+"F5.wireOp",EDGE,"E37.MirrorCS")])],"isStart":true});
            var Q13;
            Q13=makeQuery(id+"F8.opExtrude","CAP_EDGE",EDGE,{"disambiguationData":[OSD([sQuery(id+"F5.wireOp",EDGE,"E36.MirrorCS")])],"isStart":true});
            var Q14;
            {var subQ0=sQuery(id+"F5.wireOp",EDGE,"E42.MirrorCS");var subQ1=sQuery(id+"F5.wireOp",EDGE,"E41.MirrorCS");var subQ2=sQuery(id+"F5.wireOp",EDGE,"E40.MirrorCS");var subQ3=sQuery(id+"F5.wireOp",EDGE,"E32.MirrorCS");var subQ4=sQuery(id+"F5.wireOp",EDGE,"E27");var subQ5=sQuery(id+"F5.wireOp",EDGE,"E26");var subQ6=sQuery(id+"F5.wireOp",EDGE,"E25");var subQ7=sQuery(id+"F5.wireOp",EDGE,"E16");var subQ8=sQuery(id+"F5.wireOp",EDGE,"E46");var subQ9=sQuery(id+"F5.wireOp",EDGE,"E45");var subQ10=sQuery(id+"F5.wireOp",EDGE,"E44.5");var subQ11=sQuery(id+"F5.wireOp",EDGE,"E44.4");var subQ12=sQuery(id+"F5.wireOp",EDGE,"E44.3");var subQ13=sQuery(id+"F5.wireOp",EDGE,"E44.2");var subQ14=sQuery(id+"F5.wireOp",EDGE,"E44.1");var subQ15=sQuery(id+"F5.wireOp",EDGE,"E44.0");Q14=makeQuery(id+"F8.boolean.opBoolean","MERGE",FACE,{"derivedFrom":[makeQuery(id+"F7.boolean.opBoolean","MERGE",FACE,{"derivedFrom":[makeQuery(id+"F6.opExtrude","CAP_FACE",FACE,{"disambiguationData":[OSD([sQuery(id+"F5.wireOp",EDGE,"E14"),sQuery(id+"F5.wireOp",EDGE,"E15"),subQ7,subQ6,subQ5,sQuery(id+"F5.wireOp",EDGE,"E30.MirrorCS"),sQuery(id+"F5.wireOp",EDGE,"E31.MirrorCS"),subQ3,subQ2,subQ1,subQ15,subQ14,subQ13,subQ12,subQ11,subQ10,subQ9,subQ8,sQuery(id+"F5.wireOp",EDGE,"E48"),sQuery(id+"F5.wireOp",EDGE,"E49"),sQuery(id+"F5.wireOp",EDGE,"E50.MirrorC")])],"isStart":false}),makeQuery(id+"F7.opExtrude","CAP_FACE",FACE,{"disambiguationData":[OSD([sQuery(id+"F5.wireOp",EDGE,"E23"),sQuery(id+"F5.wireOp",EDGE,"E24"),subQ4,sQuery(id+"F5.wireOp",EDGE,"E38.MirrorCS"),sQuery(id+"F5.wireOp",EDGE,"E39.MirrorCS"),subQ0,subQ15,subQ14,subQ13,subQ12,subQ11,subQ10,subQ9,subQ8])],"isStart":false})]}),makeQuery(id+"F8.opExtrude","CAP_FACE",FACE,{"disambiguationData":[OSD([subQ7,sQuery(id+"F5.wireOp",EDGE,"E17"),sQuery(id+"F5.wireOp",EDGE,"E18"),sQuery(id+"F5.wireOp",EDGE,"E19"),sQuery(id+"F5.wireOp",EDGE,"E20"),sQuery(id+"F5.wireOp",EDGE,"E21"),sQuery(id+"F5.wireOp",EDGE,"E22"),subQ6,subQ5,subQ4])],"isStart":true}),makeQuery(id+"F8.opExtrude","CAP_FACE",FACE,{"disambiguationData":[OSD([subQ3,sQuery(id+"F5.wireOp",EDGE,"E33.MirrorCS"),sQuery(id+"F5.wireOp",EDGE,"E34.MirrorCS"),sQuery(id+"F5.wireOp",EDGE,"E35.MirrorCS"),sQuery(id+"F5.wireOp",EDGE,"E36.MirrorCS"),sQuery(id+"F5.wireOp",EDGE,"E37.MirrorCS"),subQ2,subQ1,subQ0,sQuery(id+"F5.wireOp",EDGE,"E43.MirrorCS")])],"isStart":true})]});}
            var Q15;
            {var subQ0=sQuery(id+"F5.wireOp",EDGE,"E32.MirrorCS");Q15=makeQuery(id+"F8.boolean.opBoolean","MERGE",EDGE,{"derivedFrom":[makeQuery(id+"F6.opExtrude","CAP_EDGE",EDGE,{"disambiguationData":[OSD([subQ0])],"isStart":false}),makeQuery(id+"F8.opExtrude","CAP_EDGE",EDGE,{"disambiguationData":[OSD([subQ0])],"isStart":true})]});}
            fillet(context, id + "F10", {"entities" : qUnion([Q0, Q1, Q2, Q3, Q4, Q5, Q6, Q7, Q8, Q9, Q10, Q11, Q12, Q13, Q14, Q15]), "radius" : 0.5 * mm, "tangentPropagation" : true, "allowEdgeOverflow" : false});
        }
    });
